# Revit family: Roxtec R UG frames
name_source: partatom
category: Duct Accessories
revit_build: Autodesk Revit 2017 (Build: 20190508_0315(x64)
units: mm (PartAtom-declared; Revit-internal decimal feet)

## family parameters
Cut with Voids When Loaded = No
Host = Face
Part Type = Attaches To
Round Connector Dimension = Use Diameter
Shared = No

## types (3) — shared parameters
Description = Sealing solutions for cables and pipes
ETIM Classification = EC000220
Fitting material = Steel
Fitting thickness = 5 mm  [stored 0.0164042 ft]
Frame material = Roxylon black
Manufacturer = Roxtec
Sealing height = 65 mm  [stored 0.213255 ft]
Sealing material = Roxylon black
URL = https://www.roxtec.com
Version = 2.0
zero-valued in all types: Default Elevation, NominalDepth, NominalHeight

## per-type parameters (varying)
| type | Front fitting diameter | Packing space | Sähkönumero | Wall opening diameter | Weight (kg) |
| R 200 UG | 205 mm | 120 mm  [stored 0.393701 ft] | 1753186 | 200 mm  [stored 0.656168 ft] | 3.1 |
| R 150 UG | 155 mm | 90 mm  [stored 0.295276 ft] | 1753185 | 150 mm | 1.9 |
| R 100 UG | 105 mm  [stored 0.344488 ft] | 60 mm  [stored 0.19685 ft] | 1753184 | 100 mm  [stored 0.328084 ft] | 0.8 |

note: [stored X ft] marks values corroborated as IEEE doubles in the binary element streams (Revit-internal decimal feet)

## geometry (parser evidence)
native form markers: Sweep x2
no freeform markers — native parametric forms only
